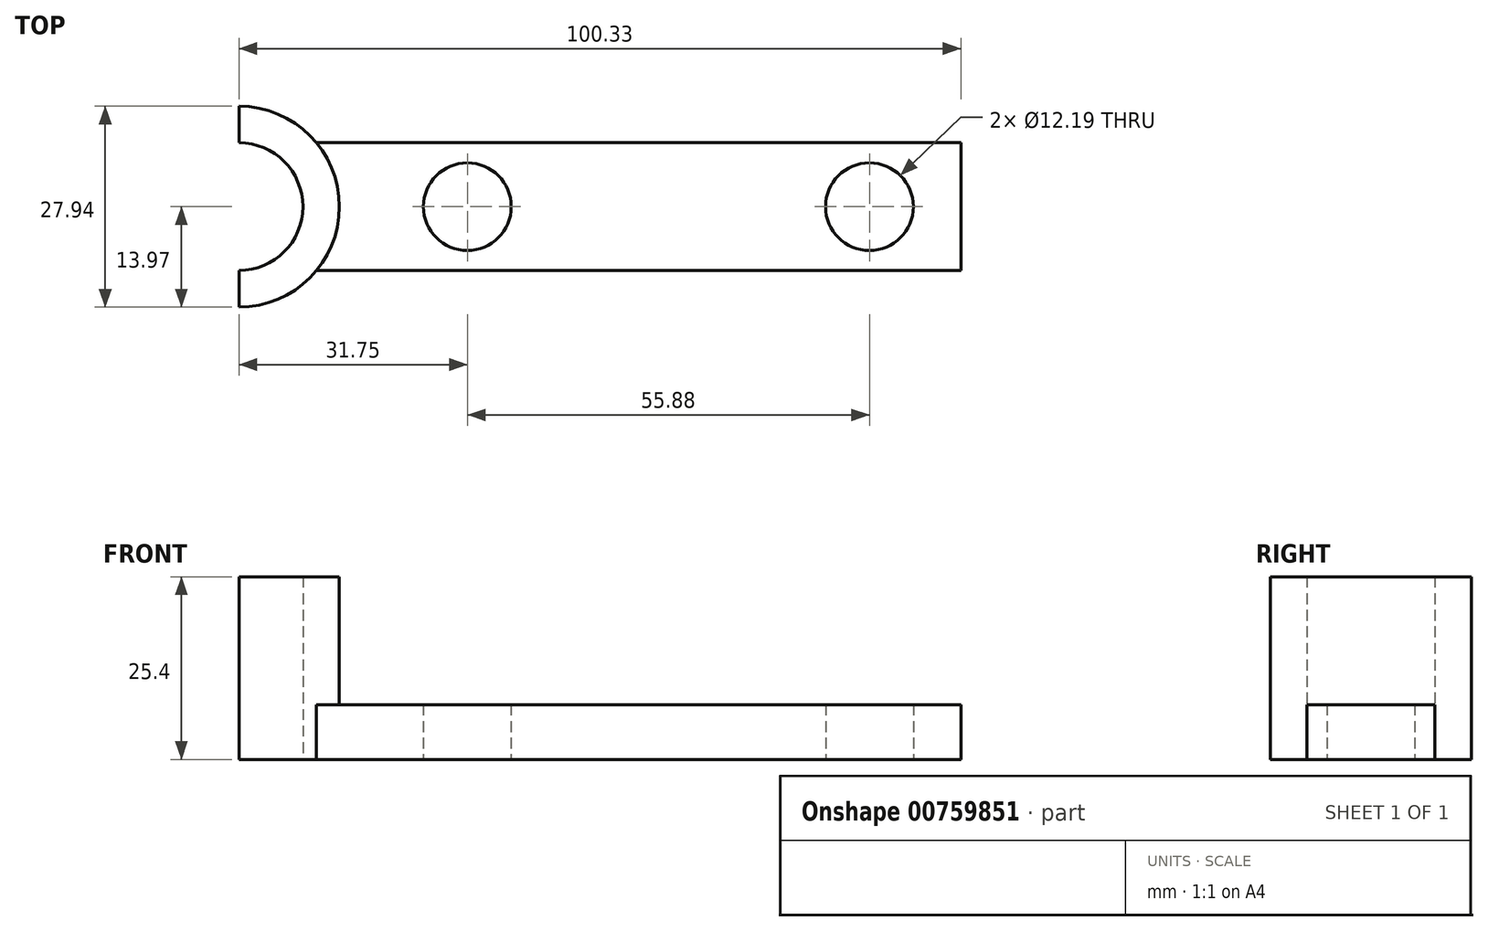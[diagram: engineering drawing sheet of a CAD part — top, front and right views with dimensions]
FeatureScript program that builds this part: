
annotation { "Feature Type Name" : "Feature", "Feature Type Description" : "" }
export const myFeature = defineFeature(function(context is Context, id is Id, definition is map)
    precondition{}
    {
        {
            var Q0;
            Q0=qCreatedBy(makeId("Top.planeOp"),FACE);
            var sketch = newSketch(context, id + "F0", { "sketchPlane" : qUnion([Q0])});
            skArc(sketch, "E0", {"start": v(0, -8.9) * mm, "mid": v(8.9, 0) * mm, "end": v(0, 8.9) * mm});
            skArc(sketch, "E1", {"start": v(0, -13.97) * mm, "mid": v(13.97, 0) * mm, "end": v(0, 13.97) * mm});
            skLineSegment(sketch, "E2", {"start": v(0, 13.97) * mm, "end": v(0, 8.89) * mm});
            skLineSegment(sketch, "E3.trimOffspring", {"start": v(0, -8.89) * mm, "end": v(0, -13.97) * mm});
            skSolve(sketch);
        }
        {
            var Q0;
            Q0 = qSketchRegion(id + "F0", true);
            var Q1;
            Q1=makeQuery(id+"F0.imprint","IMPRINT",FACE,{"disambiguationData":[TD([[makeQuery(id+"F0.imprint","IMPRINT",EDGE,{"derivedFrom":sQuery(id+"F0.wireOp",EDGE,"E0")}),-1.0]])]});
            extrude(context, id + "F1", {"entities" : qUnion([Q0, Q1]), "depth" : 25.4 * mm, "offsetDistance" : 25.4 * mm});
        }
        {
            var Q0;
            Q0=makeQuery(id+"F1.opExtrude","CAP_FACE",FACE,{"disambiguationData":[OSD([sQuery(id+"F0.wireOp",EDGE,"E0"),sQuery(id+"F0.wireOp",EDGE,"E1"),sQuery(id+"F0.wireOp",EDGE,"E2"),sQuery(id+"F0.wireOp",EDGE,"E3.trimOffspring")])],"isStart":true});
            var sketch = newSketch(context, id + "F2", { "sketchPlane" : qUnion([Q0])});
            skLineSegment(sketch, "E4", {"start": v(0, 8.9) * mm, "end": v(100.33, 8.9) * mm});
            skLineSegment(sketch, "E5", {"start": v(100.33, 8.9) * mm, "end": v(100.33, -8.89) * mm});
            skLineSegment(sketch, "E6", {"start": v(100.33, -8.89) * mm, "end": v(0, -8.9) * mm});
            skCircle(sketch, "E7", {"center": v(31.75, 0) * mm, "radius": 6.1 * mm});
            skCircle(sketch, "E8", {"center": v(87.63, 0) * mm, "radius": 6.1 * mm});
            skSolve(sketch);
        }
        {
            var Q0;
            {var subQ1=sQuery(id+"F2.wireOp",EDGE,"E5");Q0=makeQuery(id+"F2.imprint","IMPRINT",FACE,{"disambiguationData":[TD([[makeQuery(id+"F2.imprint","IMPRINT",EDGE,{"derivedFrom":subQ1}),-1.0]])]});}
            extrude(context, id + "F3", {"entities" : qUnion([Q0]), "operationType" : NewBodyOperationType.ADD, "oppositeDirection" : true, "depth" : 7.62 * mm, "offsetDistance" : 25.4 * mm});
        }
    });
